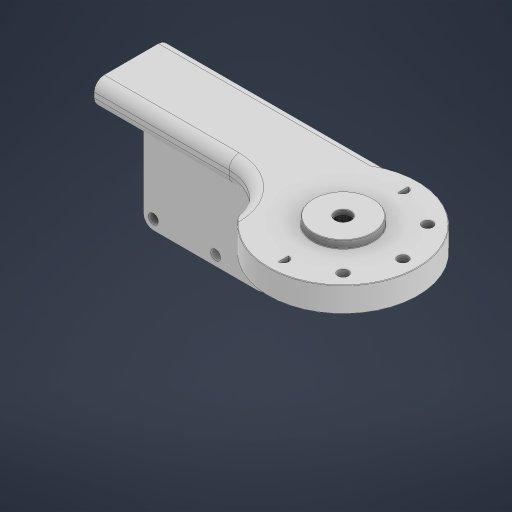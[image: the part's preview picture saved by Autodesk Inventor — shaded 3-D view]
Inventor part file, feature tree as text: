
AUTODESK INVENTOR PART (.ipt)
format: ipt  version: 2023 (Build 270158000, 158)  size: 471,040 bytes
history: native  units: in
note: dims shown in document units (in); Inventor stores cm internally (conversion verified against a paired STEP export)
features: extrude x4, sketch x3, fillet x2, other x1
ambient origin geometry x8: Origin, YZ Plane, XZ Plane, XY Plane, X Axis, Y Axis, Z Axis, Center Point
bodies: Solid1 (feature_tree)
feature tree (10):
  sketch  "Sketch1"  dims[d0=1.9685in d1=1.1732in]
  extrude  "Extrusion1"  Depth=1.1732in
  extrude  "Extrusion2"  Depth=0.1969in TaperAngle=0.0deg
  fillet  "Fillet1"  Radius=0.3937in
  extrude  "Extrusion5"  Depth=0.1969in
  fillet  "Fillet3"  Radius=0.9843in
  extrude  "Extrusion6"  Depth=0.0787in
  sketch  "Sketch4"  dims[d2=0.3937in d3=0.0in d4=0.1969in d5=0.0in d6=0.3937in]
  sketch  "Sketch5"  dims[d20=0.9843in d21=0.1969in d22=0.9843in d23=0.0in d24=0.0787in d25=0.0787in d26=0.8268in d27=0.0787in d28=0.4921in d29=0.0787in d30=0.0787in d31=0.9843in d32=0.0in]
  other  "Répétition circulaire3"
